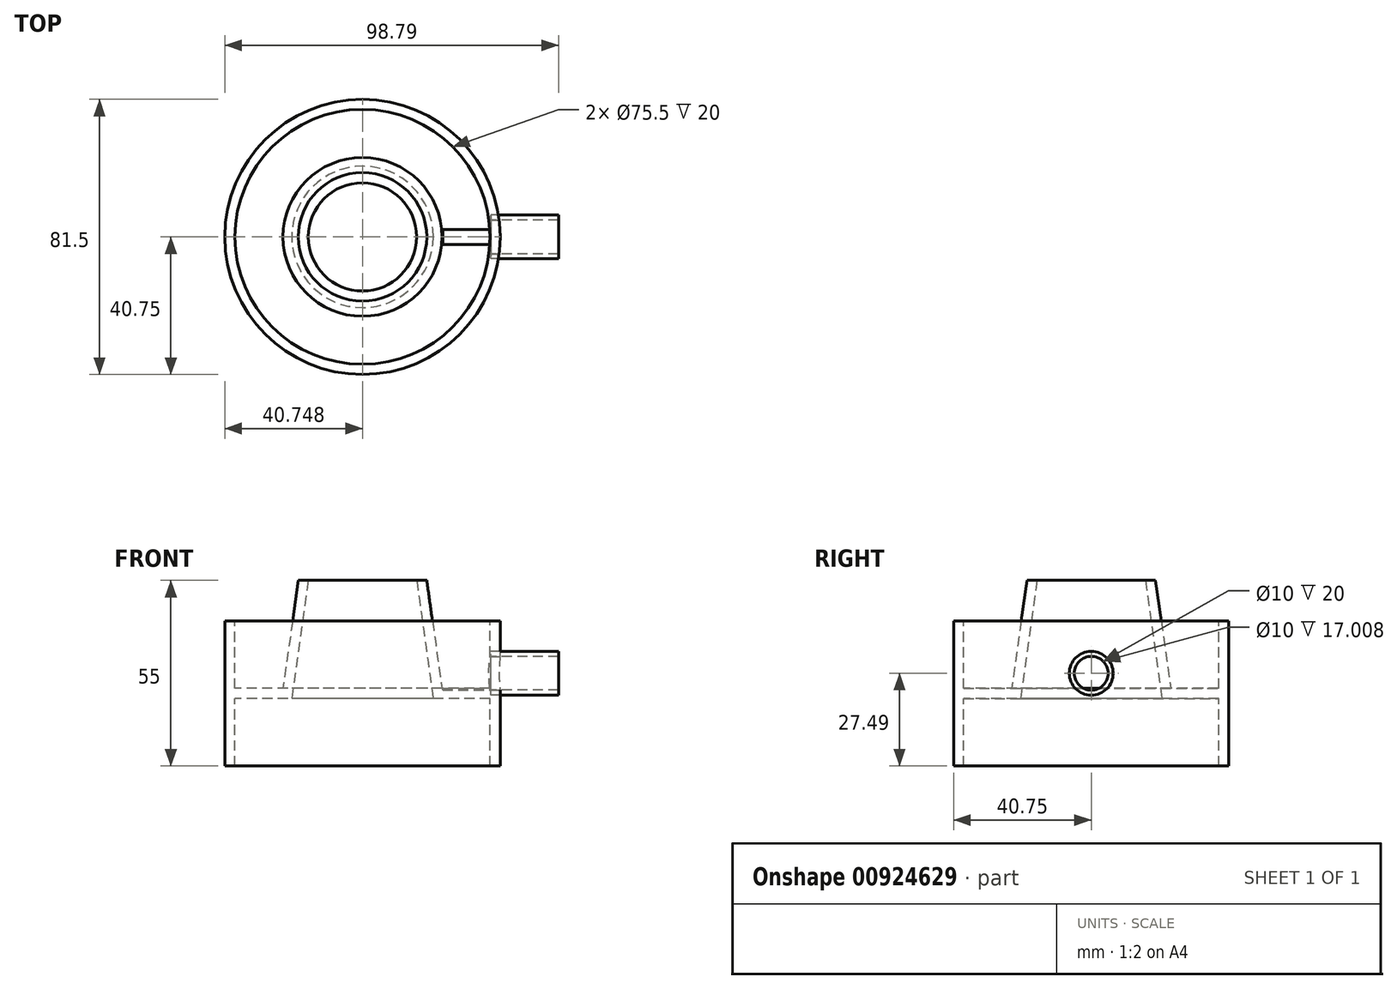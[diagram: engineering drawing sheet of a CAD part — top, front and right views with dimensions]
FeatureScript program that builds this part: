
annotation { "Feature Type Name" : "Feature", "Feature Type Description" : "" }
export const myFeature = defineFeature(function(context is Context, id is Id, definition is map)
    precondition{}
    {
        {
            var Q0;
            Q0=qCreatedBy(makeId("Front.planeOp"),FACE);
            var sketch = newSketch(context, id + "F0", { "sketchPlane" : qUnion([Q0])});
            skLineSegment(sketch, "E0", {"start": v(-133.01, 91.73) * mm, "end": v(-130.01, 91.73) * mm});
            skLineSegment(sketch, "E1", {"start": v(-130.01, 91.73) * mm, "end": v(-125.52, 59.73) * mm});
            skLineSegment(sketch, "E2", {"start": v(-125.52, 59.73) * mm, "end": v(-111.3, 59.73) * mm});
            skLineSegment(sketch, "E3", {"start": v(-111.3, 59.73) * mm, "end": v(-111.3, 79.73) * mm});
            skLineSegment(sketch, "E4", {"start": v(-111.3, 79.73) * mm, "end": v(-108.3, 79.73) * mm});
            skLineSegment(sketch, "E5", {"start": v(-108.3, 79.73) * mm, "end": v(-108.3, 36.73) * mm});
            skLineSegment(sketch, "E6", {"start": v(-108.3, 36.73) * mm, "end": v(-111.3, 36.73) * mm});
            skLineSegment(sketch, "E7", {"start": v(-111.3, 36.73) * mm, "end": v(-111.3, 56.73) * mm});
            skLineSegment(sketch, "E8", {"start": v(-111.3, 56.73) * mm, "end": v(-128.1, 56.73) * mm});
            skLineSegment(sketch, "E9", {"start": v(-128.1, 56.73) * mm, "end": v(-133.01, 91.73) * mm});
            skLineSegment(sketch, "E10", {"start": v(-149.04, 87.8) * mm, "end": v(-149.04, 20.46) * mm, "construction": true});
            skSolve(sketch);
        }
        {
            var Q0;
            Q0 = qSketchRegion(id + "F0", true);
            var Q1;
            Q1=sQuery(id+"F0.wireOp",EDGE,"E10");
            revolve(context, id + "F1", {"surfaceOperationType" : NewSurfaceOperationType.NEW, "entities" : qUnion([Q0]), "axis" : qUnion([Q1]), "revolveType" : RevolveType.FULL});
        }
        {
            var Q0;
            Q0=qCreatedBy(makeId("Right.planeOp"),FACE);
            cPlane(context, id + "F2", {"entities" : qUnion([Q0]), "cplaneType" : CPlaneType.OFFSET, "offset" : 111 * mm, "oppositeDirection" : true, "width" : 150 * mm, "height" : 150 * mm});
        }
        {
            var Q0;
            Q0=qCreatedBy(id+"F2.planeOp",FACE);
            var sketch = newSketch(context, id + "F3", { "sketchPlane" : qUnion([Q0])});
            skCircle(sketch, "E11", {"center": v(0, 64.22) * mm, "radius": 5 * mm});
            skCircle(sketch, "E12", {"center": v(0, 64.22) * mm, "radius": 6.5 * mm});
            skSolve(sketch);
        }
        {
            var Q0;
            Q0 = qSketchRegion(id + "F3", true);
            extrude(context, id + "F4", {"entities" : qUnion([Q0]), "depth" : 20 * mm, "offsetDistance" : 25 * mm});
        }
        {
            var Q0;
            Q0=makeQuery(id+"F3.imprint","IMPRINT",FACE,{"disambiguationData":[TD([[makeQuery(id+"F3.imprint","IMPRINT",EDGE,{"derivedFrom":sQuery(id+"F3.wireOp",EDGE,"E11")}),1.0]])]});
            extrude(context, id + "F5", {"entities" : qUnion([Q0]), "operationType" : NewBodyOperationType.REMOVE, "oppositeDirection" : true, "depth" : 28.6 * mm, "offsetDistance" : 25 * mm, "symmetric" : true});
        }
    });
